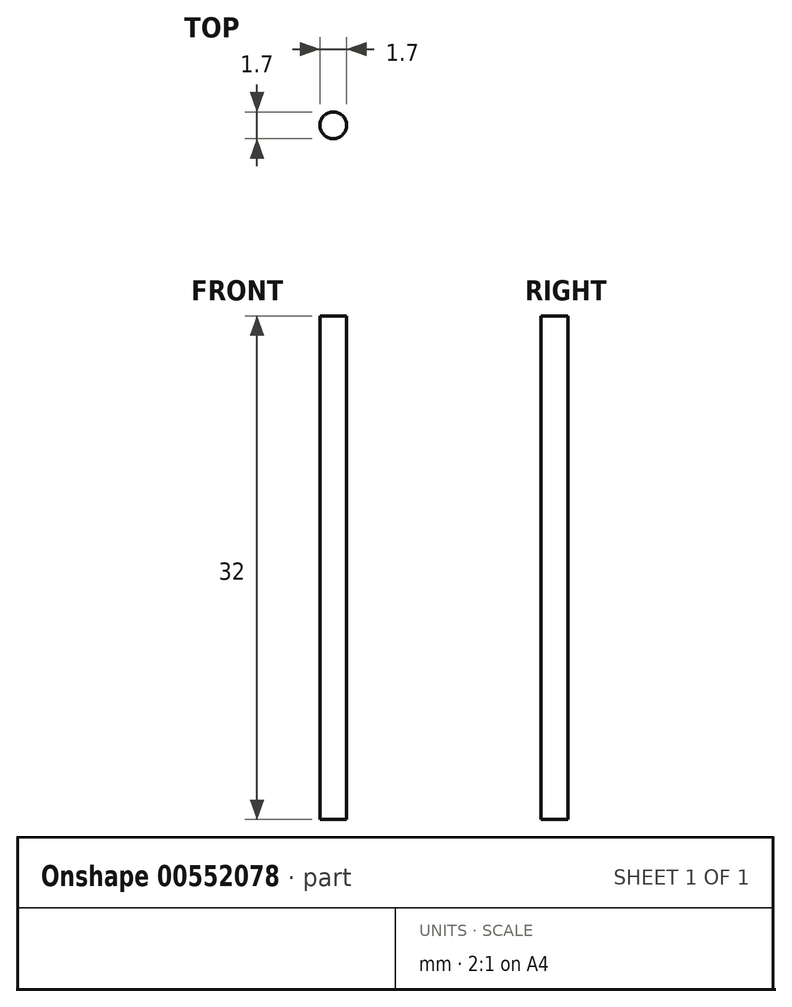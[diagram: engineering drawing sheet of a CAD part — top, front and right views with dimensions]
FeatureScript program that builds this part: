
annotation { "Feature Type Name" : "Feature", "Feature Type Description" : "" }
export const myFeature = defineFeature(function(context is Context, id is Id, definition is map)
    precondition{}
    {
        {
            var Q0;
            Q0=qCreatedBy(makeId("Top.planeOp"),FACE);
            var sketch = newSketch(context, id + "F0", { "sketchPlane" : qUnion([Q0])});
            skCircle(sketch, "E0", {"center": v(0, 0) * mm, "radius": 0.85 * mm});
            skSolve(sketch);
        }
        {
            var Q0;
            Q0=makeQuery(id+"F0.imprint","IMPRINT",FACE,{"disambiguationData":[TD([[makeQuery(id+"F0.imprint","IMPRINT",EDGE,{"derivedFrom":sQuery(id+"F0.wireOp",EDGE,"E0")}),1.0]])]});
            extrude(context, id + "F1", {"entities" : qUnion([Q0]), "depth" : 32 * mm, "offsetDistance" : 25 * mm});
        }
    });
